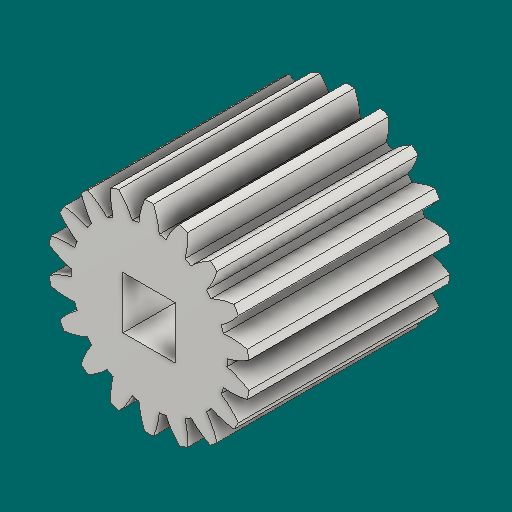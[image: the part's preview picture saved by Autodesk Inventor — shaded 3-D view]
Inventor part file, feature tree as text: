
AUTODESK INVENTOR PART (.ipt)
format: ipt  version: 2023.1 (Build 271208000, 208)  size: 336,384 bytes
history: native  units: in
note: dims shown in document units (in); Inventor stores cm internally (conversion verified against a paired STEP export)
features: other x12, sketch x5, plane x3
ambient origin geometry x8: Origin, YZ Plane, XZ Plane, XY Plane, X Axis, Y Axis, Z Axis, Center Point
bodies: Solid1 (feature_tree)
feature tree (20):
  other  "Spur Gear1"
  other  "Solid1::Spur Gear1"
  other  "TaggingFeature1"
  sketch  "Sketch1"  dims[d0=0.3937in]
  sketch  "Sketch2"  dims[d9=0.0in]
  sketch  "Sketch3"  dims[d14=0.0in]
  sketch  "Sketch4"  dims[d15=0.9in]
  sketch  "Sketch5"  dims[d16=0.0in d17=0.0in d18=0.0in d19=0.9in]
  plane  "XZ Plane_1"
  plane  "Work Plane2"
  plane  "Work Plane3"
  other  "Srf1"
  other  "Srf1::Derived"
  other  "Start plane iMate"
  other  "Distance iMate"
  other  "Position iMate"
  other  "Mesh iMate"
  other  "Axis iMate"
  other  "Mesh iMate2"
  other  "Align iMate"
